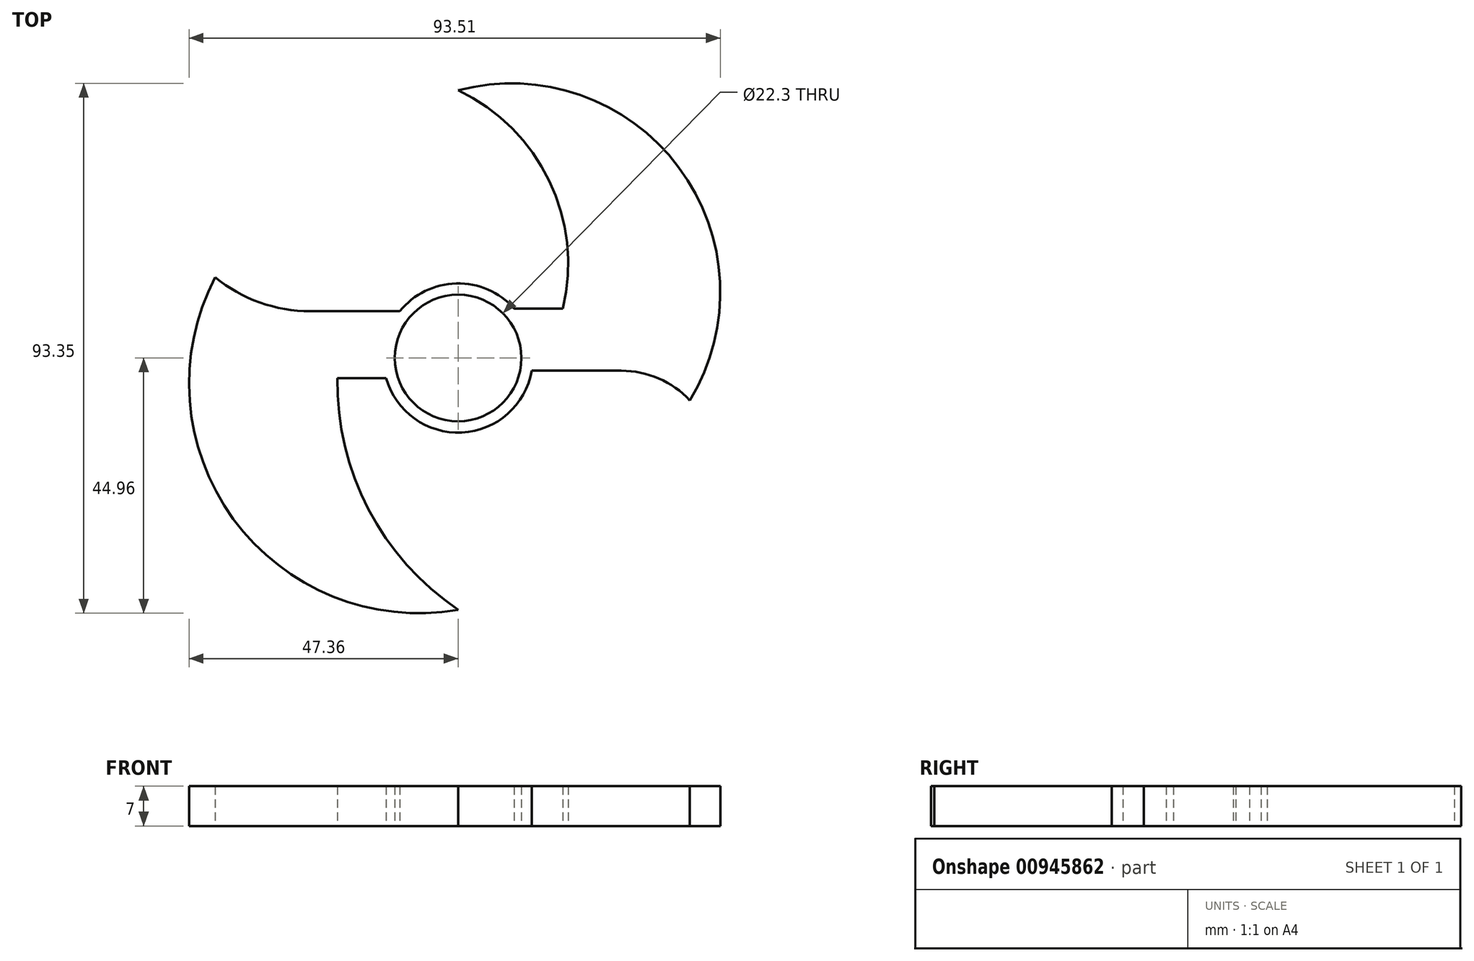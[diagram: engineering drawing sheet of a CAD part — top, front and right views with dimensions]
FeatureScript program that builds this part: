
annotation { "Feature Type Name" : "Feature", "Feature Type Description" : "" }
export const myFeature = defineFeature(function(context is Context, id is Id, definition is map)
    precondition{}
    {
        {
            var Q0;
            Q0=qCreatedBy(makeId("Top.planeOp"),FACE);
            var sketch = newSketch(context, id + "F0", { "sketchPlane" : qUnion([Q0])});
            skCircle(sketch, "E0", {"center": v(0, 0) * mm, "radius": 11.15 * mm});
            skCircle(sketch, "E1.0", {"center": v(0, 0) * mm, "radius": 13.15 * mm});
            skArc(sketch, "E2", {"start": v(40.8, -7.47) * mm, "mid": v(38.84, 33.62) * mm, "end": v(0, 47.17) * mm});
            skArc(sketch, "E3", {"start": v(18.43, 8.73) * mm, "mid": v(16.05, 31.22) * mm, "end": v(0, 47.17) * mm});
            skLineSegment(sketch, "E4", {"start": v(18.43, 8.73) * mm, "end": v(9.84, 8.73) * mm});
            skLineSegment(sketch, "E5", {"start": v(-10.24, 8.25) * mm, "end": v(-26.03, 8.25) * mm});
            skArc(sketch, "E6", {"start": v(-42.77, 14.22) * mm, "mid": v(-34.91, 9.78) * mm, "end": v(-26.03, 8.25) * mm});
            skArc(sketch, "E7", {"start": v(-42.77, 14.22) * mm, "mid": v(-39.58, -28.36) * mm, "end": v(0, -44.36) * mm});
            skArc(sketch, "E8", {"start": v(-21.25, -3.57) * mm, "mid": v(-15.78, -26.65) * mm, "end": v(0, -44.36) * mm});
            skLineSegment(sketch, "E9", {"start": v(-21.25, -3.57) * mm, "end": v(-12.66, -3.57) * mm});
            skArc(sketch, "E10", {"start": v(40.8, -7.47) * mm, "mid": v(35.32, -3.6) * mm, "end": v(28.74, -2.25) * mm});
            skLineSegment(sketch, "E11", {"start": v(28.74, -2.25) * mm, "end": v(12.96, -2.25) * mm});
            skSolve(sketch);
        }
        {
            var Q0;
            {var subQ0=sQuery(id+"F0.wireOp",EDGE,"E5");Q0=makeQuery(id+"F0.imprint","IMPRINT",FACE,{"disambiguationData":[TD([[makeQuery(id+"F0.imprint","IMPRINT",EDGE,{"derivedFrom":subQ0}),1.0]])]});}
            var Q1;
            Q1=makeQuery(id+"F0.imprint","IMPRINT",FACE,{"disambiguationData":[TD([[makeQuery(id+"F0.imprint","IMPRINT",EDGE,{"derivedFrom":sQuery(id+"F0.wireOp",EDGE,"E0")}),-1.0]])]});
            var Q2;
            {var subQ0=sQuery(id+"F0.wireOp",EDGE,"4zAlgChD-NDxh-y5i8-998E-r7BqkuHoduh7");Q2=makeQuery(id+"F0.imprint","IMPRINT",FACE,{"disambiguationData":[TD([[makeQuery(id+"F0.imprint","IMPRINT",EDGE,{"derivedFrom":subQ0}),1.0]])]});}
            var Q3;
            Q3=makeQuery(id+"F0.imprint","IMPRINT",FACE,{"disambiguationData":[TD([[makeQuery(id+"F0.imprint","IMPRINT",EDGE,{"derivedFrom":sQuery(id+"F0.wireOp",EDGE,"E2")}),1.0]])]});
            extrude(context, id + "F1", {"entities" : qUnion([Q0, Q1, Q2, Q3]), "depth" : 7 * mm, "offsetDistance" : 25 * mm});
        }
    });
